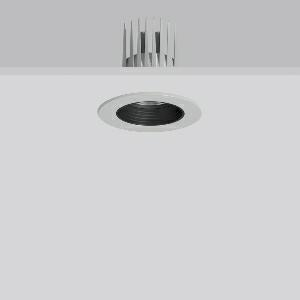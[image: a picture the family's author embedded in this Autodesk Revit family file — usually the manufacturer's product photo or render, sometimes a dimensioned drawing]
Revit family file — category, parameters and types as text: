
# Revit family: heledon_mini_e_901755_004_76_6ef0
name_source: partatom
category: Lighting Fixtures
units: mm (PartAtom-declared; Revit-internal decimal feet)

## family parameters
Cut with Voids When Loaded = No
Host = Face
Light Source = No
Part Type = Normal
Room Calculation Point = No
Round Connector Dimension = Use Diameter
Shared = No

## types (1)
- HELEDON mini E (1 x LED Modul 930, 2750 lm, 3000)
    Apparent Load = 29 VA
    Approval mark = CE
    CIE Flux Codes = 95 100 100 100 100
    Color Rendering = 90
    Color Temperature = 3000
    Default Elevation = 1800 mm
    Description = Series: HELEDON mini
Round recessed downlight. Housing: die-cast aluminium, powder-coated. Black plastic ring and recessed LED to prevent glare from the side. Optical assembly with lens made of plastic (polycarbonate) for the best homogeneous light distribution - can be changed without tools. Best colour rendering index Ra>90. Suitable for Recessed ceiling mounting. Installation without tools thanks to spring fastening system. Including separate LED converter with connecting cable 600 mm.High quality converter without flickering and stroboscopic effect. Through-wiring box (5 pole) available as accessory. The following accessories can be mounted without use of tools: interchangeable lenses, decorative glasses, honeycomb louvre, clear and frosted diffusers, white interchangeable plastic ring. 
Colour: silver
Diameter: 124 mm
Height: 3 mm
Cut-out diameter: 114 mm
Recess height: 170 mm
Luminaire: recess height: 120 mm
Lamp: LED
Socket: without socket
Colour temperature: 3000K
Colour rendering index (CRI): 92
System power: 29 W
Rated luminous flux: 2750 lm
Luminous efficiency: 95 lm/W
Control gear: Converter, dimmable, DALI
Protection class: II
Type of protection: IP 20
    Height = 0 mm  [stored 0 ft]
    Lamp = 1 x LED Modul 930
    Lamp Light Flux = 2750 lm
    Lamp count = 1
    Length = 124 mm  [stored 0.406824 ft]
    Lifetime = 50000 h
    Luminous efficacy = 95 lm/W
    Manufacturer = RZB
    ModVariant = No
    Model = 901755.004.76
    Mounting Place = Ceiling
    Mounting Type = Recessed
    Number of Poles = 1
    OnlyDefault = Yes
    Power Factor = 1
    Product Name = HELEDON mini E
    Product group = Recessed downlights
    ProductGroupID = 402
    Protection Class = Protection class II
    Protection Degree = IP 20
    RLX_Detail_Level = 1
    RLX_Emergency_Light_Flux = 0 lm
    RLX_Emergency_Type = 0
    RLX_Emergency_Type_DB = No
    RlxData = <blob elided: 134297 chars, md5=0640da25>
    Socket = socket
    Standby Power = 0 W
    System Light Flux = 2750 lm
    System Power = 29 W
    Type Comments = Product without accessories
    Type Image = 901656.004.jpg
    URL = http://relux.com
    VarID = ---
    Voltage = 230 V
    Voltage Range = 220-240 V
    Weight = 0.00 kg
    Width = 0 mm  [stored 0 ft]

note: [stored X ft] marks values corroborated as IEEE doubles in the binary element streams (Revit-internal decimal feet)

## geometry (parser evidence)
native form markers: Blend x4, Sweep x10
no freeform markers — native parametric forms only
